# Revit family: HL_Трап для внутренних помещений_HL510NPr
name_source: partatom
category: Instalační zařizovací předměty
revit_build: Autodesk Revit 2016 (Build: 20151007_0715(x64)
units: mm (PartAtom-declared; Revit-internal decimal feet)

## family parameters
Bod výpočtu místnosti = Ano
Kóta kulaté spojky = Použít průměr
Nadpis OmniClass = Deck Waste Water Drains
Ořezat dutým tvarem při načtení = Ne
Sdílené = Ano
Typ součásti = Normální
Vždy vertikální = Ano
Založené na pracovní rovině = Ne
Číslo OmniClass = 23.70.50.21.24.14

## types (1)
- HL510NPr
    EAN = 9003076004737
    Klíčová poznámka = HL510NPr
    Komentáře k typům = HL510NPr Трап для внутренних помещений DN40/50 горизонтальный с запахозапирающим устройством Primus, 123х123мм/115х115мм
    Model = HL510NPr
    Popis = Трапы для внутренних помещений
    Připojení CW = Ne
    Připojení HW = Ne
    Připojení odpadu = Ano
    Připojení ventilace = Ne
    URL = http://www.hutterer-lechner.com
    Výrobce = HL Hutterer & Lechner GmbH
    ВЕС = 0,74 [kg]
    ВЫСОТА МОНТАЖА = 91 mm
    МАКСИМАЛЬНАЯ НАГРУЗКА КЛАССА = K3 - 300 kg
    МАТЕРИАЛ = PE
    НАСАДКА = 12-70 mm / 123 x 123 mm / PP
    ПРОИЗВОДИТЕЛЬНОСТЬ = 0,50 l/s
    ПРОПУСКНАЯ СПОСОБНОСТЬ = 0.5 L/s
    РАЗМЕР = DN40/50
    РЕШЁТКА = 115 x 115 mm / V2A

## geometry (parser evidence)
native form markers: Sweep x40
no freeform markers — native parametric forms only
